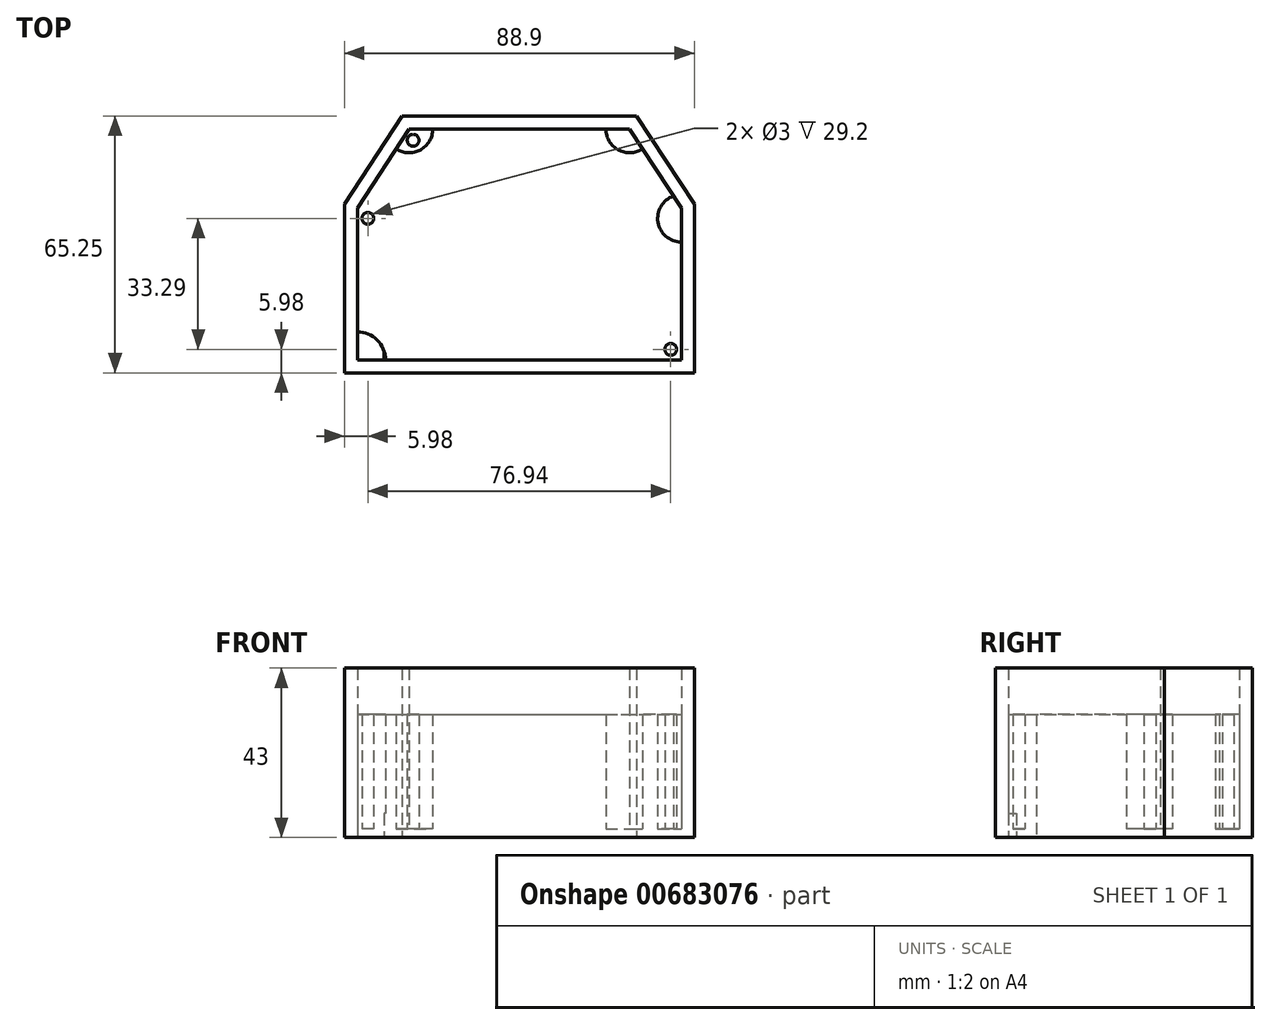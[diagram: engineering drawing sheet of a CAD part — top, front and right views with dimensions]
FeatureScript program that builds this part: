
annotation { "Feature Type Name" : "Feature", "Feature Type Description" : "" }
export const myFeature = defineFeature(function(context is Context, id is Id, definition is map)
    precondition{}
    {
        {
            var Q0;
            Q0=qCreatedBy(makeId("Top.planeOp"),FACE);
            var sketch = newSketch(context, id + "F0", { "sketchPlane" : qUnion([Q0])});
            skLineSegment(sketch, "E0.bottom", {"start": v(0, 48.45) * mm, "end": v(34.1, 48.45) * mm, "construction": true});
            skLineSegment(sketch, "E0.top", {"start": v(0, 0) * mm, "end": v(34.1, 0) * mm, "construction": true});
            skLineSegment(sketch, "E0.left", {"start": v(0, 48.45) * mm, "end": v(0, 0) * mm, "construction": true});
            skLineSegment(sketch, "E0.right", {"start": v(34.1, 48.45) * mm, "end": v(34.1, 0) * mm, "construction": true});
            skLineSegment(sketch, "E1", {"start": v(17.05, 48.45) * mm, "end": v(17.05, 0) * mm, "construction": true});
            skLineSegment(sketch, "E2", {"start": v(34.1, 10) * mm, "end": v(37.4, 10) * mm});
            skLineSegment(sketch, "E3", {"start": v(37.4, 10) * mm, "end": v(37.4, 0) * mm});
            skLineSegment(sketch, "E4", {"start": v(37.4, 0) * mm, "end": v(17.05, 0) * mm});
            skLineSegment(sketch, "E5.MirrorCS", {"start": v(0, 10) * mm, "end": v(-3.3, 10) * mm});
            skLineSegment(sketch, "E6.MirrorCS", {"start": v(-3.3, 0) * mm, "end": v(17.05, 0) * mm});
            skLineSegment(sketch, "E7.MirrorCS", {"start": v(-3.3, 10) * mm, "end": v(-3.3, 0) * mm});
            skLineSegment(sketch, "E8", {"start": v(0, 10) * mm, "end": v(0, 0) * mm});
            skLineSegment(sketch, "E9", {"start": v(34.1, 10) * mm, "end": v(34.1, 0) * mm});
            skLineSegment(sketch, "E10", {"start": v(4.58, 48.45) * mm, "end": v(29.52, 48.45) * mm});
            skLineSegment(sketch, "E11", {"start": v(4.58, 48.45) * mm, "end": v(4.58, 38.45) * mm});
            skLineSegment(sketch, "E12", {"start": v(4.58, 38.45) * mm, "end": v(1.28, 38.45) * mm});
            skLineSegment(sketch, "E13", {"start": v(1.28, 38.45) * mm, "end": v(1.28, 48.45) * mm});
            skLineSegment(sketch, "E14", {"start": v(1.28, 48.45) * mm, "end": v(4.58, 48.45) * mm});
            skLineSegment(sketch, "E15.MirrorCS", {"start": v(29.52, 38.45) * mm, "end": v(32.82, 38.45) * mm});
            skLineSegment(sketch, "E16.MirrorCS", {"start": v(32.82, 48.45) * mm, "end": v(29.52, 48.45) * mm});
            skLineSegment(sketch, "E17.MirrorCS", {"start": v(29.52, 48.45) * mm, "end": v(29.52, 38.45) * mm});
            skLineSegment(sketch, "E18.MirrorCS", {"start": v(32.82, 38.45) * mm, "end": v(32.82, 48.45) * mm});
            skLineSegment(sketch, "E19.bottom", {"start": v(32.82, 48.45) * mm, "end": v(19.52, 48.45) * mm});
            skLineSegment(sketch, "E19.top", {"start": v(32.82, 51.75) * mm, "end": v(19.52, 51.75) * mm});
            skLineSegment(sketch, "E19.left", {"start": v(32.82, 48.45) * mm, "end": v(32.82, 51.75) * mm});
            skLineSegment(sketch, "E19.right", {"start": v(19.52, 48.45) * mm, "end": v(19.52, 51.75) * mm});
            skLineSegment(sketch, "E20.MirrorCS", {"start": v(1.28, 48.45) * mm, "end": v(14.58, 48.45) * mm});
            skLineSegment(sketch, "E21.MirrorCS", {"start": v(1.28, 48.45) * mm, "end": v(1.28, 51.75) * mm});
            skLineSegment(sketch, "E22.MirrorCS", {"start": v(14.58, 48.45) * mm, "end": v(14.58, 51.75) * mm});
            skLineSegment(sketch, "E23.MirrorCS", {"start": v(1.28, 51.75) * mm, "end": v(14.58, 51.75) * mm});
            skSolve(sketch);
        }
        {
            var Q0;
            Q0=qCreatedBy(makeId("Top.planeOp"),FACE);
            var sketch = newSketch(context, id + "F1", { "sketchPlane" : qUnion([Q0])});
            skLineSegment(sketch, "E24", {"start": v(0, 0) * mm, "end": v(-30.9, 0) * mm, "construction": true});
            skLineSegment(sketch, "E25.bottom", {"start": v(-7.6, 0) * mm, "end": v(-27.6, 0) * mm, "construction": true});
            skLineSegment(sketch, "E25.top", {"start": v(-7.6, 45.5) * mm, "end": v(-27.6, 45.5) * mm, "construction": true});
            skLineSegment(sketch, "E25.left", {"start": v(-7.6, 0) * mm, "end": v(-7.6, 45.5) * mm, "construction": true});
            skLineSegment(sketch, "E25.right", {"start": v(-27.6, 0) * mm, "end": v(-27.6, 45.5) * mm, "construction": true});
            skLineSegment(sketch, "E26.bottom", {"start": v(-7.6, 0) * mm, "end": v(-4.3, 0) * mm});
            skLineSegment(sketch, "E26.top", {"start": v(-7.6, 10) * mm, "end": v(-4.3, 10) * mm});
            skLineSegment(sketch, "E26.left", {"start": v(-7.6, 0) * mm, "end": v(-7.6, 10) * mm});
            skLineSegment(sketch, "E26.right", {"start": v(-4.3, 0) * mm, "end": v(-4.3, 10) * mm});
            skLineSegment(sketch, "E27", {"start": v(-17.6, 45.5) * mm, "end": v(-17.6, 0) * mm, "construction": true});
            skLineSegment(sketch, "E28", {"start": v(-7.6, 22.75) * mm, "end": v(-27.6, 22.75) * mm, "construction": true});
            skLineSegment(sketch, "E29.MirrorCS", {"start": v(-30.9, 0) * mm, "end": v(-30.9, 10) * mm});
            skLineSegment(sketch, "E30.MirrorCS", {"start": v(-27.6, 0) * mm, "end": v(-27.6, 10) * mm});
            skLineSegment(sketch, "E31.MirrorCS", {"start": v(-27.6, 10) * mm, "end": v(-30.9, 10) * mm});
            skLineSegment(sketch, "E32.MirrorCS", {"start": v(-27.6, 0) * mm, "end": v(-30.9, 0) * mm});
            skLineSegment(sketch, "E33.MirrorCS", {"start": v(-7.6, 35.5) * mm, "end": v(-4.3, 35.5) * mm});
            skLineSegment(sketch, "E34.MirrorCS", {"start": v(-7.6, 45.5) * mm, "end": v(-4.3, 45.5) * mm});
            skLineSegment(sketch, "E35.MirrorCS", {"start": v(-4.3, 45.5) * mm, "end": v(-4.3, 35.5) * mm});
            skLineSegment(sketch, "E36.MirrorCS", {"start": v(-7.6, 45.5) * mm, "end": v(-7.6, 35.5) * mm});
            skLineSegment(sketch, "E37.MirrorCS", {"start": v(-27.6, 45.5) * mm, "end": v(-27.6, 35.5) * mm});
            skLineSegment(sketch, "E38.MirrorCS", {"start": v(-30.9, 45.5) * mm, "end": v(-30.9, 35.5) * mm});
            skLineSegment(sketch, "E39.MirrorCS", {"start": v(-27.6, 35.5) * mm, "end": v(-30.9, 35.5) * mm});
            skLineSegment(sketch, "E40.MirrorCS", {"start": v(-27.6, 45.5) * mm, "end": v(-30.9, 45.5) * mm});
            skLineSegment(sketch, "E41.bottom", {"start": v(-4.3, 45.5) * mm, "end": v(-12.3, 45.5) * mm});
            skLineSegment(sketch, "E41.top", {"start": v(-4.3, 48.8) * mm, "end": v(-12.3, 48.8) * mm});
            skLineSegment(sketch, "E41.left", {"start": v(-4.3, 45.5) * mm, "end": v(-4.3, 48.8) * mm});
            skLineSegment(sketch, "E41.right", {"start": v(-12.3, 45.5) * mm, "end": v(-12.3, 48.8) * mm});
            skLineSegment(sketch, "E42.MirrorCS", {"start": v(-30.9, 45.5) * mm, "end": v(-30.9, 48.8) * mm});
            skLineSegment(sketch, "E43.MirrorCS", {"start": v(-30.9, 45.5) * mm, "end": v(-22.9, 45.5) * mm});
            skLineSegment(sketch, "E44.MirrorCS", {"start": v(-30.9, 48.8) * mm, "end": v(-22.9, 48.8) * mm});
            skLineSegment(sketch, "E45.MirrorCS", {"start": v(-22.9, 45.5) * mm, "end": v(-22.9, 48.8) * mm});
            skSolve(sketch);
        }
        {
            var Q0;
            Q0=qCreatedBy(makeId("Top.planeOp"),FACE);
            var sketch = newSketch(context, id + "F2", { "sketchPlane" : qUnion([Q0])});
            skLineSegment(sketch, "E46.bottom", {"start": v(-37.75, 38.65) * mm, "end": v(44.55, 38.65) * mm, "construction": true});
            skLineSegment(sketch, "E46.top", {"start": v(-37.75, 0) * mm, "end": v(44.55, 0) * mm, "construction": true});
            skLineSegment(sketch, "E46.left", {"start": v(-37.75, 38.65) * mm, "end": v(-37.75, 0) * mm, "construction": true});
            skLineSegment(sketch, "E46.right", {"start": v(44.55, 38.65) * mm, "end": v(44.55, 0) * mm, "construction": true});
            skCircle(sketch, "E47", {"center": v(41.87, 2.68) * mm, "radius": 1.5 * mm});
            skLineSegment(sketch, "E48", {"start": v(41.87, 1.18) * mm, "end": v(41.87, 0) * mm, "construction": true});
            skLineSegment(sketch, "E49", {"start": v(43.37, 2.68) * mm, "end": v(44.55, 2.68) * mm, "construction": true});
            skLineSegment(sketch, "E50", {"start": v(44.55, 19.32) * mm, "end": v(-37.75, 19.32) * mm, "construction": true});
            skLineSegment(sketch, "E51", {"start": v(3.4, 38.65) * mm, "end": v(3.4, 0) * mm, "construction": true});
            skLineSegment(sketch, "E52", {"start": v(43.37, 2.68) * mm, "end": v(41.87, 2.68) * mm, "construction": true});
            skLineSegment(sketch, "E53.MirrorCS", {"start": v(43.37, 35.97) * mm, "end": v(41.87, 35.97) * mm, "construction": true});
            skCircle(sketch, "E54.MirrorC", {"center": v(41.87, 35.97) * mm, "radius": 1.5 * mm});
            skCircle(sketch, "E55.MirrorC", {"center": v(-35.07, 2.68) * mm, "radius": 1.5 * mm});
            skCircle(sketch, "E56.MirrorC", {"center": v(-35.07, 35.97) * mm, "radius": 1.5 * mm});
            skLineSegment(sketch, "E57", {"start": v(3.4, 38.65) * mm, "end": v(3.4, 58.65) * mm, "construction": true});
            skSolve(sketch);
        }
        {
            var Q0;
            Q0=qCreatedBy(makeId("Top.planeOp"),FACE);
            var sketch = newSketch(context, id + "F3", { "sketchPlane" : qUnion([Q0])});
            skCircle(sketch, "E58", {"center": v(-14.6, 46.4) * mm, "radius": 7.75 * mm, "construction": true});
            skLineSegment(sketch, "E59", {"start": v(3.4, 38.65) * mm, "end": v(3.4, 65) * mm, "construction": true});
            skCircle(sketch, "E60.MirrorC", {"center": v(21.4, 46.4) * mm, "radius": 7.75 * mm, "construction": true});
            skSolve(sketch);
        }
        {
            var Q0;
            Q0=qCreatedBy(makeId("Top.planeOp"),FACE);
            var sketch = newSketch(context, id + "F4", { "sketchPlane" : qUnion([Q0])});
            skLineSegment(sketch, "E61.bottom", {"start": v(44.55, 0) * mm, "end": v(-37.75, 0) * mm});
            skLineSegment(sketch, "E61.left", {"start": v(44.55, 0) * mm, "end": v(44.55, 36.95) * mm});
            skLineSegment(sketch, "E61.right", {"start": v(-37.75, 0) * mm, "end": v(-37.75, 38.65) * mm});
            skLineSegment(sketch, "E62", {"start": v(3.4, 58.65) * mm, "end": v(3.4, 65) * mm, "construction": true});
            skLineSegment(sketch, "E63", {"start": v(3.4, 58.65) * mm, "end": v(-24.6, 58.65) * mm});
            skLineSegment(sketch, "E64", {"start": v(-24.6, 58.65) * mm, "end": v(-37.75, 38.65) * mm});
            skLineSegment(sketch, "E65.MirrorCS", {"start": v(31.4, 58.65) * mm, "end": v(44.55, 38.65) * mm});
            skLineSegment(sketch, "E66.MirrorCS", {"start": v(3.4, 58.65) * mm, "end": v(31.4, 58.65) * mm});
            skLineSegment(sketch, "E67.0", {"start": v(2.5, 61.95) * mm, "end": v(-26.38, 61.95) * mm});
            skLineSegment(sketch, "E67.1", {"start": v(2.5, 61.95) * mm, "end": v(33.18, 61.95) * mm});
            skLineSegment(sketch, "E67.2", {"start": v(-41.05, -3.3) * mm, "end": v(-41.05, 39.64) * mm});
            skLineSegment(sketch, "E67.3", {"start": v(47.85, -3.3) * mm, "end": v(-41.05, -3.3) * mm});
            skLineSegment(sketch, "E67.4", {"start": v(47.85, -3.3) * mm, "end": v(47.85, 39.64) * mm});
            skLineSegment(sketch, "E67.5", {"start": v(-26.38, 61.95) * mm, "end": v(-41.05, 39.64) * mm});
            skLineSegment(sketch, "E67.6", {"start": v(33.18, 61.95) * mm, "end": v(47.85, 39.64) * mm});
            skCircle(sketch, "E68", {"center": v(30.38, 55.83) * mm, "radius": 1.5 * mm});
            skArc(sketch, "E69", {"start": v(34.7, 53.64) * mm, "mid": v(28.55, 53.37) * mm, "end": v(25.4, 58.65) * mm});
            skCircle(sketch, "E70.MirrorC", {"center": v(-23.58, 55.83) * mm, "radius": 1.5 * mm});
            skArc(sketch, "E71.MirrorCS", {"start": v(-27.9, 53.64) * mm, "mid": v(-21.75, 53.37) * mm, "end": v(-18.6, 58.65) * mm});
            skArc(sketch, "E72", {"start": v(44.55, 7.15) * mm, "mid": v(39.5, 5.06) * mm, "end": v(37.4, 0) * mm});
            skArc(sketch, "E73.MirrorCS", {"start": v(-37.75, 7.15) * mm, "mid": v(-32.7, 5.06) * mm, "end": v(-30.6, 0) * mm});
            skArc(sketch, "E74", {"start": v(44.55, 29.97) * mm, "mid": v(38.63, 34.97) * mm, "end": v(42.58, 41.64) * mm});
            skArc(sketch, "E75.MirrorCS", {"start": v(-37.75, 29.97) * mm, "mid": v(-31.83, 34.97) * mm, "end": v(-35.78, 41.64) * mm});
            skLineSegment(sketch, "E76", {"start": v(44.55, 35.97) * mm, "end": v(41.87, 35.97) * mm, "construction": true});
            skSolve(sketch);
        }
        {
            var Q0;
            {var subQ4=sQuery(id+"F4.wireOp",EDGE,"E69");Q0=makeQuery(id+"F4.imprint","IMPRINT",FACE,{"disambiguationData":[TD([[makeQuery(id+"F4.imprint","IMPRINT",EDGE,{"derivedFrom":subQ4}),1.0]])]});}
            cPlane(context, id + "F5", {"entities" : qUnion([Q0]), "cplaneType" : CPlaneType.OFFSET, "offset" : 2.1 * mm, "width" : 150 * mm, "height" : 150 * mm});
        }
        {
            var Q0;
            Q0=qCreatedBy(id+"F5.planeOp",FACE);
            var sketch = newSketch(context, id + "F6", { "sketchPlane" : qUnion([Q0])});
            skCircle(sketch, "E77.0", {"center": v(41.87, 2.68) * mm, "radius": 1.5 * mm});
            skArc(sketch, "E78.0", {"start": v(44.55, 7.15) * mm, "mid": v(39.5, 5.06) * mm, "end": v(37.4, 0) * mm});
            skLineSegment(sketch, "E79.0", {"start": v(44.55, 0) * mm, "end": v(44.55, 36.95) * mm});
            skLineSegment(sketch, "E80.0", {"start": v(44.55, 0) * mm, "end": v(-37.75, 0) * mm});
            skArc(sketch, "E81.0", {"start": v(-37.75, 7.15) * mm, "mid": v(-32.7, 5.06) * mm, "end": v(-30.6, 0) * mm});
            skLineSegment(sketch, "E82.0", {"start": v(-37.75, 0) * mm, "end": v(-37.75, 38.65) * mm});
            skCircle(sketch, "E83.0", {"center": v(-35.07, 2.68) * mm, "radius": 1.5 * mm});
            skArc(sketch, "E84.0", {"start": v(-37.75, 29.97) * mm, "mid": v(-31.83, 34.97) * mm, "end": v(-35.78, 41.64) * mm});
            skCircle(sketch, "E85.0", {"center": v(-35.07, 35.97) * mm, "radius": 1.5 * mm});
            skLineSegment(sketch, "E86.0", {"start": v(-24.6, 58.65) * mm, "end": v(-37.75, 38.65) * mm});
            skLineSegment(sketch, "E87.0", {"start": v(3.4, 58.65) * mm, "end": v(-24.6, 58.65) * mm});
            skCircle(sketch, "E88.0", {"center": v(-23.58, 55.83) * mm, "radius": 1.5 * mm});
            skArc(sketch, "E89.0", {"start": v(-27.9, 53.64) * mm, "mid": v(-21.75, 53.37) * mm, "end": v(-18.6, 58.65) * mm});
            skLineSegment(sketch, "E90.0", {"start": v(2.5, 61.95) * mm, "end": v(33.18, 61.95) * mm});
            skLineSegment(sketch, "E91.0", {"start": v(3.4, 58.65) * mm, "end": v(31.4, 58.65) * mm});
            skLineSegment(sketch, "E92.0", {"start": v(2.5, 61.95) * mm, "end": v(-26.38, 61.95) * mm});
            skLineSegment(sketch, "E93.0", {"start": v(-26.38, 61.95) * mm, "end": v(-41.05, 39.64) * mm});
            skLineSegment(sketch, "E94.0", {"start": v(-41.05, -3.3) * mm, "end": v(-41.05, 39.64) * mm});
            skLineSegment(sketch, "E95.0", {"start": v(47.85, -3.3) * mm, "end": v(-41.05, -3.3) * mm});
            skLineSegment(sketch, "E96.0", {"start": v(47.85, -3.3) * mm, "end": v(47.85, 39.64) * mm});
            skArc(sketch, "E97.0", {"start": v(44.55, 29.97) * mm, "mid": v(38.63, 34.97) * mm, "end": v(42.58, 41.64) * mm});
            skCircle(sketch, "E98.0", {"center": v(41.87, 35.97) * mm, "radius": 1.5 * mm});
            skLineSegment(sketch, "E99.0", {"start": v(33.18, 61.95) * mm, "end": v(47.85, 39.64) * mm});
            skLineSegment(sketch, "E100.0", {"start": v(31.4, 58.65) * mm, "end": v(44.55, 38.65) * mm});
            skArc(sketch, "E101.0", {"start": v(34.7, 53.64) * mm, "mid": v(28.55, 53.37) * mm, "end": v(25.4, 58.65) * mm});
            skCircle(sketch, "E102.0", {"center": v(30.38, 55.83) * mm, "radius": 1.5 * mm});
            skLineSegment(sketch, "E103", {"start": v(44.55, 38.65) * mm, "end": v(44.55, 36.95) * mm});
            skSolve(sketch);
        }
        {
            var Q0;
            Q0=makeQuery(id+"F6.imprint","IMPRINT",FACE,{"disambiguationData":[TD([[makeQuery(id+"F6.imprint","IMPRINT",EDGE,{"derivedFrom":sQuery(id+"F6.wireOp",EDGE,"E77.0")}),-1.0]])]});
            var Q1;
            {var subQ0=sQuery(id+"F6.wireOp",EDGE,"E97.0");Q1=makeQuery(id+"F6.imprint","IMPRINT",FACE,{"disambiguationData":[TD([[makeQuery(id+"F6.imprint","IMPRINT",EDGE,{"derivedFrom":subQ0}),-1.0]])]});}
            var Q2;
            {var subQ3=sQuery(id+"F6.wireOp",EDGE,"E101.0");Q2=makeQuery(id+"F6.imprint","IMPRINT",FACE,{"disambiguationData":[TD([[makeQuery(id+"F6.imprint","IMPRINT",EDGE,{"derivedFrom":subQ3}),-1.0]])]});}
            var Q3;
            Q3=makeQuery(id+"F6.imprint","IMPRINT",FACE,{"disambiguationData":[TD([[makeQuery(id+"F6.imprint","IMPRINT",EDGE,{"derivedFrom":sQuery(id+"F6.wireOp",EDGE,"E88.0")}),1.0]])]});
            var Q4;
            {var subQ3=sQuery(id+"F6.wireOp",EDGE,"E84.0");Q4=makeQuery(id+"F6.imprint","IMPRINT",FACE,{"disambiguationData":[TD([[makeQuery(id+"F6.imprint","IMPRINT",EDGE,{"derivedFrom":subQ3}),1.0]])]});}
            var Q5;
            {var subQ3=sQuery(id+"F6.wireOp",EDGE,"E81.0");Q5=makeQuery(id+"F6.imprint","IMPRINT",FACE,{"disambiguationData":[TD([[makeQuery(id+"F6.imprint","IMPRINT",EDGE,{"derivedFrom":subQ3}),-1.0]])]});}
            var Q6;
            Q6=makeQuery(id+"F6.imprint","IMPRINT",FACE,{"disambiguationData":[TD([[makeQuery(id+"F6.imprint","IMPRINT",EDGE,{"derivedFrom":sQuery(id+"F6.wireOp",EDGE,"E90.0")}),-1.0]])]});
            extrude(context, id + "F7", {"entities" : qUnion([Q0, Q1, Q2, Q3, Q4, Q5, Q6]), "depth" : (25.27 + 3.93) * mm, "offsetDistance" : 25 * mm});
        }
        {
            var Q0;
            {var subQ4=sQuery(id+"F4.wireOp",EDGE,"E69");Q0=makeQuery(id+"F4.imprint","IMPRINT",FACE,{"disambiguationData":[TD([[makeQuery(id+"F4.imprint","IMPRINT",EDGE,{"derivedFrom":subQ4}),1.0]])]});}
            var Q1;
            Q1=makeQuery(id+"F4.imprint","IMPRINT",FACE,{"disambiguationData":[TD([[makeQuery(id+"F4.imprint","IMPRINT",EDGE,{"derivedFrom":sQuery(id+"F4.wireOp",EDGE,"E67.0")}),1.0]])]});
            var Q2;
            {var subQ3=sQuery(id+"F4.wireOp",EDGE,"E73.MirrorCS");Q2=makeQuery(id+"F4.imprint","IMPRINT",FACE,{"disambiguationData":[TD([[makeQuery(id+"F4.imprint","IMPRINT",EDGE,{"derivedFrom":subQ3}),-1.0]])]});}
            var Q3;
            {var subQ3=sQuery(id+"F4.wireOp",EDGE,"E75.MirrorCS");Q3=makeQuery(id+"F4.imprint","IMPRINT",FACE,{"disambiguationData":[TD([[makeQuery(id+"F4.imprint","IMPRINT",EDGE,{"derivedFrom":subQ3}),1.0]])]});}
            var Q4;
            {var subQ3=sQuery(id+"F4.wireOp",EDGE,"E74");Q4=makeQuery(id+"F4.imprint","IMPRINT",FACE,{"disambiguationData":[TD([[makeQuery(id+"F4.imprint","IMPRINT",EDGE,{"derivedFrom":subQ3}),-1.0]])]});}
            var Q5;
            Q5=makeQuery(id+"F4.imprint","IMPRINT",FACE,{"disambiguationData":[TD([[makeQuery(id+"F4.imprint","IMPRINT",EDGE,{"derivedFrom":sQuery(id+"F4.wireOp",EDGE,"E68")}),-1.0]])]});
            var Q6;
            Q6=makeQuery(id+"F4.imprint","IMPRINT",FACE,{"disambiguationData":[TD([[makeQuery(id+"F4.imprint","IMPRINT",EDGE,{"derivedFrom":sQuery(id+"F4.wireOp",EDGE,"E68")}),1.0]])]});
            var Q7;
            Q7=makeQuery(id+"F4.imprint","IMPRINT",FACE,{"disambiguationData":[TD([[makeQuery(id+"F4.imprint","IMPRINT",EDGE,{"derivedFrom":sQuery(id+"F4.wireOp",EDGE,"E70.MirrorC")}),1.0]])]});
            var Q8;
            Q8=makeQuery(id+"F4.imprint","IMPRINT",FACE,{"disambiguationData":[TD([[makeQuery(id+"F4.imprint","IMPRINT",EDGE,{"derivedFrom":sQuery(id+"F4.wireOp",EDGE,"E70.MirrorC")}),-1.0]])]});
            var Q9;
            {var subQ3=sQuery(id+"F4.wireOp",EDGE,"E72");Q9=makeQuery(id+"F4.imprint","IMPRINT",FACE,{"disambiguationData":[TD([[makeQuery(id+"F4.imprint","IMPRINT",EDGE,{"derivedFrom":subQ3}),1.0]])]});}
            extrude(context, id + "F8", {"entities" : qUnion([Q0, Q1, Q2, Q3, Q4, Q5, Q6, Q7, Q8, Q9]), "depth" : 2.1 * mm, "offsetDistance" : 25 * mm});
        }
        {
            var Q0;
            Q0=makeQuery(id+"F1.imprint","IMPRINT",FACE,{"disambiguationData":[TD([[makeQuery(id+"F1.imprint","IMPRINT",EDGE,{"derivedFrom":sQuery(id+"F1.wireOp",EDGE,"E37.MirrorCS")}),-1.0]])]});
            var Q1;
            Q1=makeQuery(id+"F1.imprint","IMPRINT",FACE,{"disambiguationData":[TD([[makeQuery(id+"F1.imprint","IMPRINT",EDGE,{"derivedFrom":sQuery(id+"F1.wireOp",EDGE,"E42.MirrorCS")}),-1.0]])]});
            var Q2;
            Q2=makeQuery(id+"F1.imprint","IMPRINT",FACE,{"disambiguationData":[TD([[makeQuery(id+"F1.imprint","IMPRINT",EDGE,{"derivedFrom":sQuery(id+"F1.wireOp",EDGE,"E29.MirrorCS")}),-1.0]])]});
            var Q3;
            Q3=makeQuery(id+"F1.imprint","IMPRINT",FACE,{"disambiguationData":[TD([[makeQuery(id+"F1.imprint","IMPRINT",EDGE,{"derivedFrom":sQuery(id+"F1.wireOp",EDGE,"E26.bottom")}),1.0]])]});
            var Q4;
            Q4=makeQuery(id+"F1.imprint","IMPRINT",FACE,{"disambiguationData":[TD([[makeQuery(id+"F1.imprint","IMPRINT",EDGE,{"derivedFrom":sQuery(id+"F1.wireOp",EDGE,"E33.MirrorCS")}),1.0]])]});
            var Q5;
            Q5=makeQuery(id+"F1.imprint","IMPRINT",FACE,{"disambiguationData":[TD([[makeQuery(id+"F1.imprint","IMPRINT",EDGE,{"derivedFrom":sQuery(id+"F1.wireOp",EDGE,"E41.top")}),1.0]])]});
            var Q6;
            Q6=makeQuery(id+"F0.imprint","IMPRINT",FACE,{"disambiguationData":[TD([[makeQuery(id+"F0.imprint","IMPRINT",EDGE,{"derivedFrom":sQuery(id+"F0.wireOp",EDGE,"E5.MirrorCS")}),1.0]])]});
            var Q7;
            {var subQ0=sQuery(id+"F0.wireOp",EDGE,"E11");Q7=makeQuery(id+"F0.imprint","IMPRINT",FACE,{"disambiguationData":[TD([[makeQuery(id+"F0.imprint","IMPRINT",EDGE,{"derivedFrom":subQ0}),-1.0]])]});}
            var Q8;
            {var subQ1=sQuery(id+"F0.wireOp",EDGE,"E21.MirrorCS");Q8=makeQuery(id+"F0.imprint","IMPRINT",FACE,{"disambiguationData":[TD([[makeQuery(id+"F0.imprint","IMPRINT",EDGE,{"derivedFrom":subQ1}),-1.0]])]});}
            var Q9;
            Q9=makeQuery(id+"F0.imprint","IMPRINT",FACE,{"disambiguationData":[TD([[makeQuery(id+"F0.imprint","IMPRINT",EDGE,{"derivedFrom":sQuery(id+"F0.wireOp",EDGE,"E19.top")}),1.0]])]});
            var Q10;
            Q10=makeQuery(id+"F0.imprint","IMPRINT",FACE,{"disambiguationData":[TD([[makeQuery(id+"F0.imprint","IMPRINT",EDGE,{"derivedFrom":sQuery(id+"F0.wireOp",EDGE,"E15.MirrorCS")}),1.0]])]});
            var Q11;
            Q11=makeQuery(id+"F0.imprint","IMPRINT",FACE,{"disambiguationData":[TD([[makeQuery(id+"F0.imprint","IMPRINT",EDGE,{"derivedFrom":sQuery(id+"F0.wireOp",EDGE,"E2")}),-1.0]])]});
            extrude(context, id + "F9", {"entities" : qUnion([Q0, Q1, Q2, Q3, Q4, Q5, Q6, Q7, Q8, Q9, Q10, Q11]), "operationType" : NewBodyOperationType.ADD, "depth" : 6.1 * mm, "offsetDistance" : 25 * mm});
        }
        {
            var Q0;
            Q0=makeQuery(id+"F6.imprint","IMPRINT",FACE,{"disambiguationData":[TD([[makeQuery(id+"F6.imprint","IMPRINT",EDGE,{"derivedFrom":sQuery(id+"F6.wireOp",EDGE,"E90.0")}),-1.0]])]});
            extrude(context, id + "F10", {"entities" : qUnion([Q0]), "operationType" : NewBodyOperationType.ADD, "depth" : (40 - 2.1 + 3) * mm, "offsetDistance" : 25 * mm});
        }
    });
